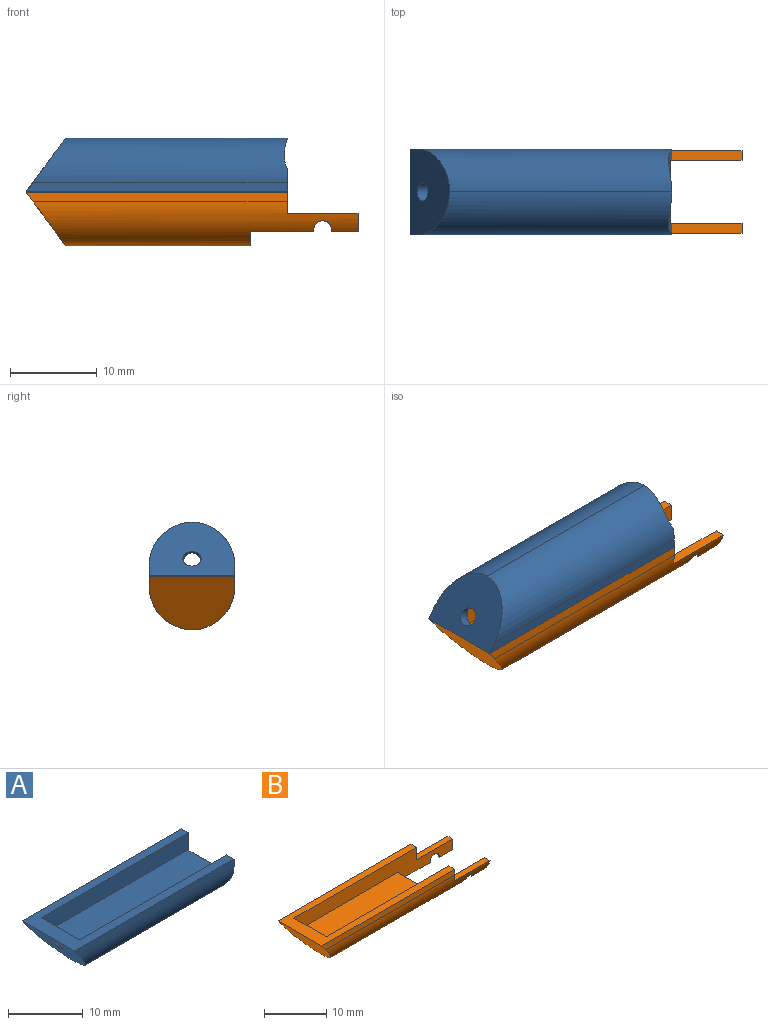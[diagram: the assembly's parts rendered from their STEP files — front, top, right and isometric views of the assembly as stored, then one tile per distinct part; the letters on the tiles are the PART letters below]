
ASSEMBLY  parts=2 mates=1
PART A: 16 faces, bbox 30.5x10.2x6.6 mm
  f0: plane 1.1x0.08mm, normal (0,0,1), area 0.1mm2, adj f1,f8,f9,f14
  f1: plane 2.46x1.27mm, normal (1,0,0), area 3mm2, adj f0,f2,f7,f9,f14
  f2: plane 30.11x9.91mm, normal (0,0,1), area 95.8mm2, adj f1,f3,f5,f6,f7,f9,f10,f12
  f3: plane 9.91x6.23mm, normal (-0.81,0,-0.59), area 59.3mm2, adj f2,f6,f7,f13,f14,f15
  f4: plane 1.17x0.08mm, normal (0,0,1), area 0.1mm2, adj f5,f8,f10,f13
  f5: plane 2.46x1.34mm, normal (1,0,0), area 3.2mm2, adj f2,f4,f6,f10,f13
  f6: plane 30.11x1.15mm, normal (0,-1,0), area 34.1mm2, adj f2,f3,f5,f13
  f7: plane 30.11x1.15mm, normal (0,1,0), area 34.1mm2, adj f1,f2,f3,f14
  f8: cylinder r=4.42mm len=9.56mm, axis (0,-1,0), area 24.6mm2, adj f0,f4,f9,f10,f11,f13,f14
  f9: plane 27.86x2.79mm, normal (0,-1,0), area 77.6mm2, adj f0,f1,f2,f8,f11,f12
  f10: plane 27.86x2.79mm, normal (0,1,0), area 77.6mm2, adj f2,f4,f5,f8,f11,f12
  f11: plane 27.72x7.29mm, normal (0,0,1), area 202.1mm2, adj f8,f9,f10,f12
  f12: plane 7.62x3.12mm, normal (1,0,0), area 16.1mm2, adj f2,f9,f10,f11,f15
  f13: cylinder r=5.08mm len=29.36mm, axis (-1,0,0), area 210.4mm2, adj f3,f4,f5,f6,f8,f14
  f14: cylinder r=5.08mm len=29.36mm, axis (1,0,0), area 210.4mm2, adj f0,f1,f3,f7,f8,f13
  f15: cylinder r=1.05mm len=2.79mm, axis (-0.81,0,-0.59), area 7.2mm2, adj f3,f12
PART B: 19 faces, bbox 38.3x9.9x6.2 mm
  f0: plane 8.17x1.1mm, normal (0,0,1), area 9mm2, adj f1,f4,f12,f17
  f1: plane 2.05x1.1mm, normal (1,0,0), area 1.3mm2, adj f0,f12,f17
  f2: plane 2.13x1.17mm, normal (1,0,0), area 1.5mm2, adj f7,f13,f16
  f3: cylinder r=1.03mm len=2.05mm, axis (0,-1,0), area 1.9mm2, adj f12,f17
  f4: plane 2.46x1.27mm, normal (1,0,0), area 3mm2, adj f0,f5,f10,f12,f17
  f5: plane 30.11x9.91mm, normal (0,0,1), area 95.8mm2, adj f4,f6,f8,f9,f10,f12,f13,f14
  f6: plane 9.91x6.23mm, normal (-0.81,0,-0.59), area 62.8mm2, adj f5,f9,f10,f16,f17
  f7: plane 8.17x1.17mm, normal (0,0,1), area 9.6mm2, adj f2,f8,f13,f16
  f8: plane 2.46x1.34mm, normal (1,0,0), area 3.2mm2, adj f5,f7,f9,f13,f16
  f9: plane 30.11x1.15mm, normal (0,-1,0), area 34.1mm2, adj f5,f6,f8,f16
  f10: plane 30.11x1.15mm, normal (0,1,0), area 34.1mm2, adj f4,f5,f6,f17
  f11: cylinder r=1.03mm len=2.05mm, axis (0,-1,0), area 2.1mm2, adj f13,f16
  f12: plane 35.95x4.51mm, normal (0,-1,0), area 99.6mm2, adj f0,f1,f3,f4,f5,f14,f15,f17
  f13: plane 35.95x4.59mm, normal (0,1,0), area 100.5mm2, adj f2,f5,f7,f8,f11,f14,f15,f16
  f14: plane 7.29x2.79mm, normal (1,0,0), area 20.4mm2, adj f5,f12,f13,f15
  f15: plane 23.52x7.29mm, normal (0,0,1), area 171.5mm2, adj f12,f13,f14,f18
  f16: cylinder r=5.08mm len=37.45mm, axis (-1,0,0), area 211.5mm2, adj f2,f6,f7,f8,f9,f11,f13,f17
  f17: cylinder r=5.08mm len=37.45mm, axis (1,0,0), area 210.4mm2, adj f0,f1,f3,f4,f6,f10,f12,f16
  f18: plane 7.29x3.43mm, normal (1,0,0), area 21.1mm2, adj f12,f13,f15,f16,f17
PLACE A rot(axis=(1,0,0),180deg) t=(4.07,-5.94,17.83)mm
PLACE B t=(4.07,3.96,5.37)mm fixed
MATE slider A.f2 <-> B.f5  axis (0,0,-1) through (-34.22,3.96,11.6)mm
